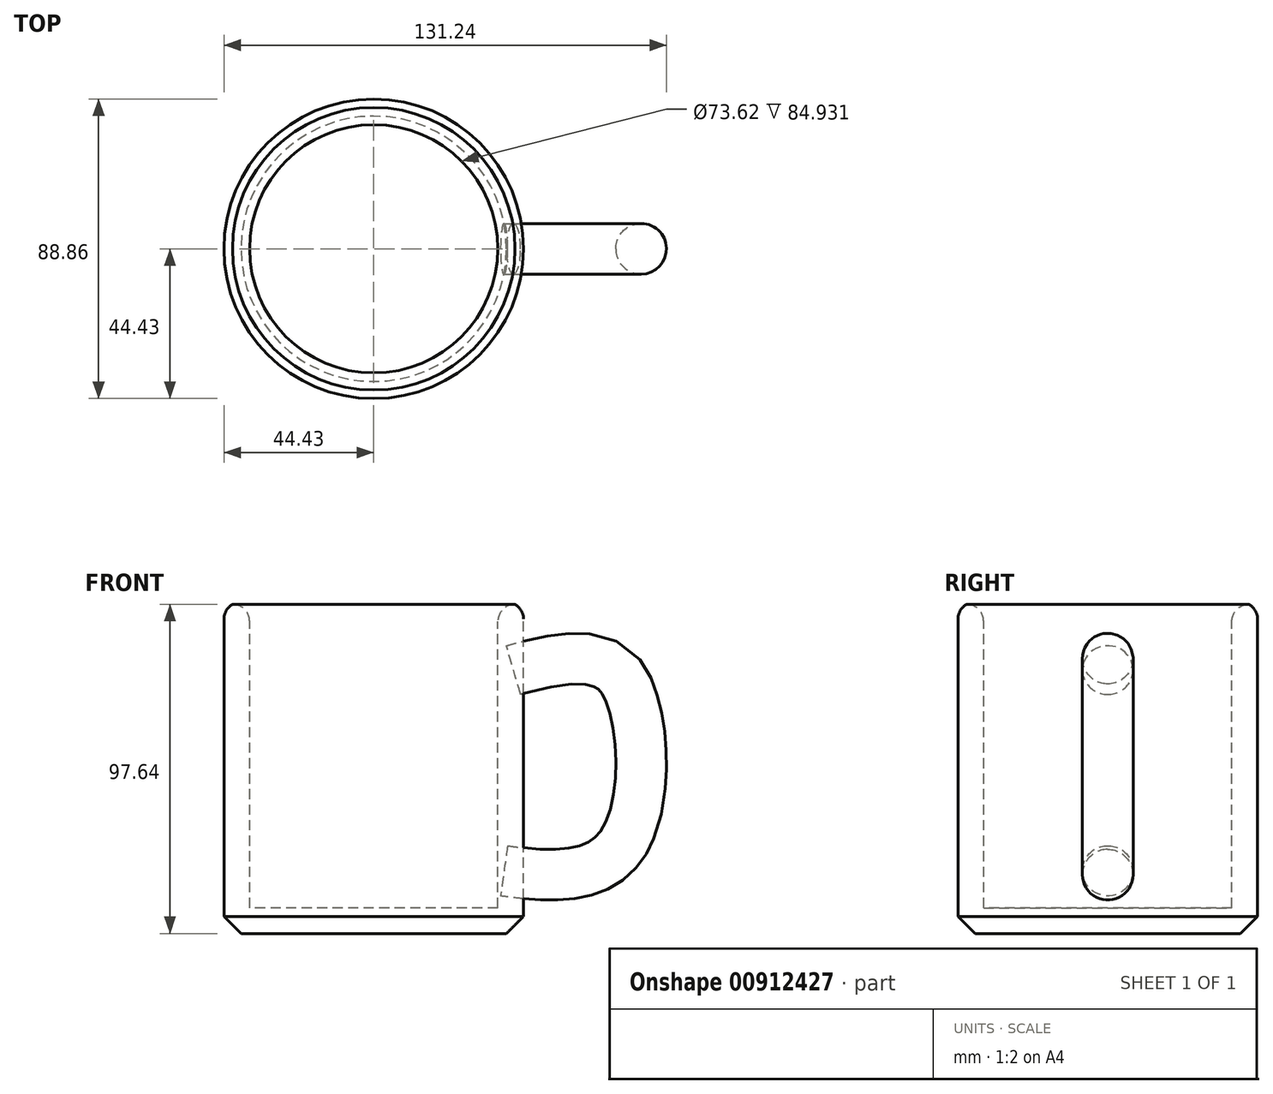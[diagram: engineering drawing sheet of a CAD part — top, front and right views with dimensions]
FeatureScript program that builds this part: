
annotation { "Feature Type Name" : "Feature", "Feature Type Description" : "" }
export const myFeature = defineFeature(function(context is Context, id is Id, definition is map)
    precondition{}
    {
        {
            var Q0;
            Q0=qCreatedBy(makeId("Right.planeOp"),FACE);
            var sketch = newSketch(context, id + "F0", { "sketchPlane" : qUnion([Q0])});
            skLineSegment(sketch, "E0.bottom", {"start": v(0, 46.26) * mm, "end": v(36.81, 46.26) * mm});
            skLineSegment(sketch, "E0.top", {"start": v(0, -43.76) * mm, "end": v(36.81, -43.76) * mm});
            skLineSegment(sketch, "E0.left", {"start": v(0, 46.26) * mm, "end": v(0, -43.76) * mm});
            skLineSegment(sketch, "E0.right", {"start": v(36.81, 46.26) * mm, "end": v(36.81, -43.76) * mm});
            skSolve(sketch);
        }
        {
            var Q0;
            Q0=makeQuery(id+"F0.imprint","IMPRINT",FACE,{"disambiguationData":[TD([[makeQuery(id+"F0.imprint","IMPRINT",EDGE,{"derivedFrom":sQuery(id+"F0.wireOp",EDGE,"E0.bottom")}),-1.0]])]});
            var Q1;
            Q1=sQuery(id+"F0.wireOp",EDGE,"E0.left");
            revolve(context, id + "F1", {"surfaceOperationType" : NewSurfaceOperationType.NEW, "entities" : qUnion([Q0]), "axis" : qUnion([Q1]), "revolveType" : RevolveType.FULL});
        }
        {
            var Q0;
            Q0=makeQuery(id+"F1.opRevolve","SWEPT_FACE",FACE,{"disambiguationData":[OSD([sQuery(id+"F0.wireOp",EDGE,"E0.bottom")])]});
            shell(context, id + "F2", {"entities" : qUnion([Q0]), "thickness" : 7.62 * mm, "oppositeDirection" : true});
        }
        {
            var Q0;
            Q0=makeQuery(id+"F2.opShell","OFFSET_EDGE",EDGE,{"disambiguationData":[OSD([sQuery(id+"F0.wireOp",EDGE,"E0.bottom"),sQuery(id+"F0.wireOp",EDGE,"E0.right")])]});
            fillet(context, id + "F3", {"entities" : qUnion([Q0]), "radius" : 5.08 * mm, "tangentPropagation" : true, "allowEdgeOverflow" : false});
        }
        {
            var Q0;
            Q0=makeQuery(id+"F1.opRevolve","SWEPT_EDGE",EDGE,{"disambiguationData":[OSD([sQuery(id+"F0.wireOp",EDGE,"E0.bottom"),sQuery(id+"F0.wireOp",EDGE,"E0.right")])]});
            fillet(context, id + "F4", {"entities" : qUnion([Q0]), "radius" : 5.08 * mm, "tangentPropagation" : true, "allowEdgeOverflow" : false});
        }
        {
            var Q0;
            Q0=makeQuery(id+"F1.opRevolve","SWEPT_EDGE",EDGE,{"disambiguationData":[OSD([sQuery(id+"F0.wireOp",EDGE,"E0.top"),sQuery(id+"F0.wireOp",EDGE,"E0.right")])]});
            chamfer(context, id + "F5", {"entities" : qUnion([Q0]), "width" : 5.08 * mm, "tangentPropagation" : true});
        }
        {
            var Q0;
            Q0=qCreatedBy(makeId("Front.planeOp"),FACE);
            var sketch = newSketch(context, id + "F6", { "sketchPlane" : qUnion([Q0])});
            skFitSpline(sketch, "E1", {"points": [v(41.45, 26.76) * mm, v(77.02, 16.77) * mm, v(72.79, -26.25) * mm, v(38.66, -32.8) * mm], "startDerivative": vector(233.68, 68.53) * mm, "endDerivative": vector(-136.7, 19.53) * mm});
            skSolve(sketch);
        }
        {
            var Q0;
            Q0=sQuery(id+"F6.wireOp",VERTEX,"E1.end");
            var Q1;
            Q1=sQuery(id+"F6.wireOp",EDGE,"E1");
            cPlane(context, id + "F7", {"entities" : qUnion([Q0, Q1]), "cplaneType" : CPlaneType.CURVE_POINT, "offset" : 25.4 * mm, "width" : 152.4 * mm, "height" : 152.4 * mm});
        }
        {
            var Q0;
            Q0=qCreatedBy(id+"F7.planeOp",FACE);
            var sketch = newSketch(context, id + "F8", { "sketchPlane" : qUnion([Q0])});
            skCircle(sketch, "E2", {"center": v(0, -27) * mm, "radius": 7.51 * mm});
            skSolve(sketch);
        }
        {
            var Q0;
            Q0=makeQuery(id+"F8.imprint","IMPRINT",FACE,{"disambiguationData":[TD([[makeQuery(id+"F8.imprint","IMPRINT",EDGE,{"derivedFrom":sQuery(id+"F8.wireOp",EDGE,"E2")}),1.0]])]});
            var Q1;
            Q1=sQuery(id+"F6.wireOp",EDGE,"E1");
            sweep(context, id + "F9", {"profiles" : qUnion([Q0]), "path" : qUnion([Q1])});
        }
    });
